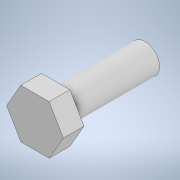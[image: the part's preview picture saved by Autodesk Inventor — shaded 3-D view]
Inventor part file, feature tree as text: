
AUTODESK INVENTOR PART (.ipt)
format: ipt  version: 2022 (Build 260153000, 153)  size: 110,592 bytes
history: native  units: mm
features: extrude x2, sketch x2
ambient origin geometry x8: Origin, YZ Plane, XZ Plane, XY Plane, X Axis, Y Axis, Z Axis, Center Point
bodies: Solid1 (feature_tree)
feature tree (4):
  extrude  "Extrusion1"  Depth=3.9mm TaperAngle=360.0deg
  extrude  "Extrusion2"  Depth=12.3mm
  sketch  "Sketch1"  dims[d0=3.9mm d1=60.0mm d3=360.0deg]
  sketch  "Sketch2"  dims[d5=2.85mm d6=0.0mm d7=4.0mm d8=12.3mm d9=0.0mm d10=0.5mm d11=0.872665mm d12=0.5mm d13=0.872665mm]
